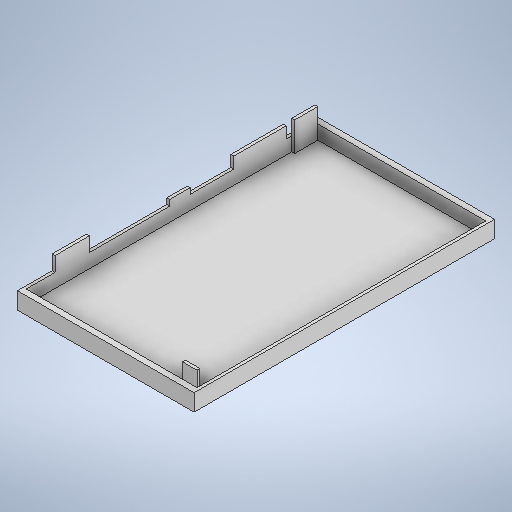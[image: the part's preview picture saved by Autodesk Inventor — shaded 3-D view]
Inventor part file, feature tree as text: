
AUTODESK INVENTOR PART (.ipt)
format: ipt  version: 2025.2 (Build 292293000, 293)  size: 315,392 bytes
history: native  units: mm
features: extrude x6, sketch x6
ambient origin geometry x8: Origin, YZ Plane, XZ Plane, XY Plane, X Axis, Y Axis, Z Axis, Center Point
bodies: Solid1 (feature_tree)
feature tree (12):
  extrude  "Extrusion1"  Depth=103.298mm
  extrude  "Extrusion2"  Depth=2.0mm
  extrude  "Extrusion3"  Depth=2.0mm
  extrude  "Extrusion4"  Depth=4.8mm TaperAngle=0.0deg
  extrude  "Extrusion5"  Depth=11.9mm
  extrude  "Extrusion6"  Depth=10.0mm
  sketch  "Sketch1"  dims[d0=60.74mm d1=103.298mm]
  sketch  "Sketch2"  dims[d2=1.0mm d3=0.0mm d4=2.0mm]
  sketch  "Sketch3"  dims[d5=1.0mm d6=2.0mm]
  sketch  "Sketch4"  dims[d7=1.0mm d8=4.8mm d9=0.0mm]
  sketch  "Sketch5"  dims[d18=11.9mm d19=11.9mm]
  sketch  "Sketch6"  dims[d20=5.0mm d21=0.0mm d22=13.2mm d23=6.0mm d24=8.4mm d25=7.0mm d26=2.0mm d27=0.0mm d28=15.0mm d29=18.0mm d30=3.9mm d31=0.0mm d32=1.0mm d33=8.0mm d34=1.0mm d35=5.0mm d36=10.0mm d37=0.0mm]
